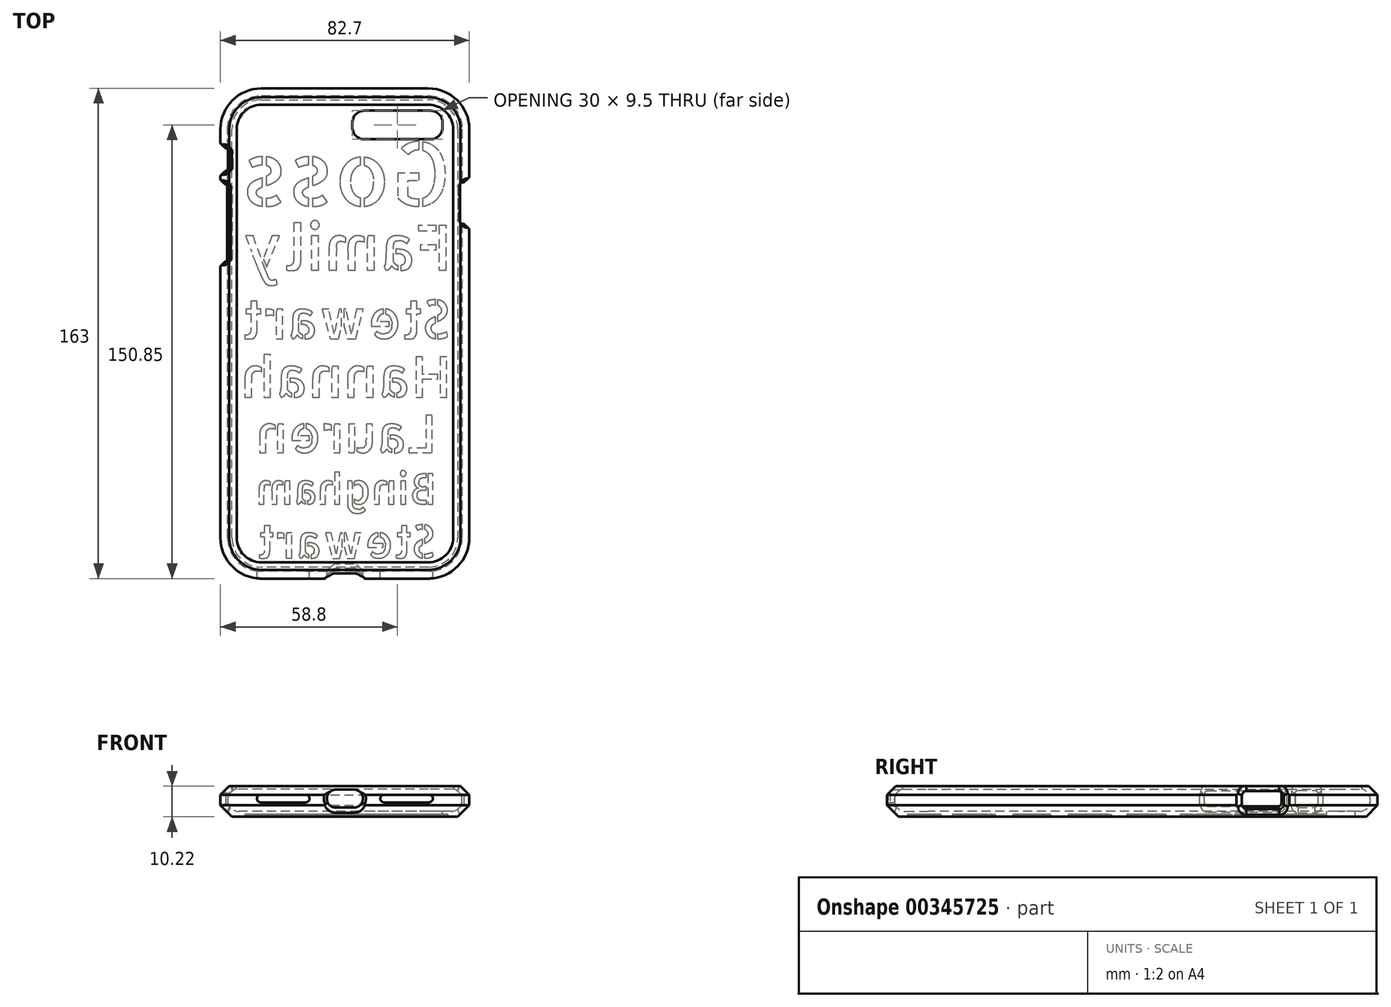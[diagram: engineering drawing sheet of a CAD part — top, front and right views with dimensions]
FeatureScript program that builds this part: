
annotation { "Feature Type Name" : "Feature", "Feature Type Description" : "" }
export const myFeature = defineFeature(function(context is Context, id is Id, definition is map)
    precondition{}
    {
        {
            assignVariable(context, id + "F0", {"name" : "HoleChamferLength", "anyValue" : 1.25});
        }
        {
            assignVariable(context, id + "F1", {"name" : "HoleChamferTopBottom", "anyValue" : 1.75});
        }
        {
            var Q0;
            Q0=qCreatedBy(makeId("Top.planeOp"),FACE);
            var sketch = newSketch(context, id + "F2", { "sketchPlane" : qUnion([Q0])});
            skLineSegment(sketch, "E0.bottom", {"start": v(27.75, 79.1) * mm, "end": v(0, 79.1) * mm});
            skLineSegment(sketch, "E0.top", {"start": v(27.75, -79.1) * mm, "end": v(-27.75, -79.1) * mm});
            skLineSegment(sketch, "E0.left", {"start": v(38.95, 67.9) * mm, "end": v(38.95, -67.9) * mm});
            skLineSegment(sketch, "E0.right", {"start": v(-38.95, 67.9) * mm, "end": v(-38.95, -67.9) * mm});
            skPoint(sketch, "E0.middle", {"position": v(0, 0) * mm});
            skPoint(sketch, "E1.visualSharp", {"position": v(-38.95, 79.1) * mm});
            skArc(sketch, "E1.filletArc", {"start": v(-27.75, 79.1) * mm, "mid": v(-35.67, 75.82) * mm, "end": v(-38.95, 67.9) * mm});
            skPoint(sketch, "E2.visualSharp", {"position": v(38.95, 79.1) * mm});
            skArc(sketch, "E2.filletArc", {"start": v(38.95, 67.9) * mm, "mid": v(35.67, 75.82) * mm, "end": v(27.75, 79.1) * mm});
            skPoint(sketch, "E3.visualSharp", {"position": v(38.95, -79.1) * mm});
            skArc(sketch, "E3.filletArc", {"start": v(27.75, -79.1) * mm, "mid": v(35.67, -75.82) * mm, "end": v(38.95, -67.9) * mm});
            skPoint(sketch, "E4.visualSharp", {"position": v(-38.95, -79.1) * mm});
            skArc(sketch, "E4.filletArc", {"start": v(-38.95, -67.9) * mm, "mid": v(-35.67, -75.82) * mm, "end": v(-27.75, -79.1) * mm});
            skLineSegment(sketch, "E5", {"start": v(0, 79.1) * mm, "end": v(-27.75, 79.1) * mm});
            skSolve(sketch);
        }
        {
            var Q0;
            Q0=qCreatedBy(makeId("Right.planeOp"),FACE);
            var sketch = newSketch(context, id + "F3", { "sketchPlane" : qUnion([Q0])});
            skPoint(sketch, "E6.0", {"position": v(79.1, 0) * mm});
            skArc(sketch, "E7", {"start": v(75.35, -3.75) * mm, "mid": v(79.1, 0) * mm, "end": v(75.35, 3.75) * mm});
            skLineSegment(sketch, "E8", {"start": v(75.35, -3.75) * mm, "end": v(75.35, 3.75) * mm, "construction": true});
            skLineSegment(sketch, "E9", {"start": v(81.5, -1.75) * mm, "end": v(81.5, 1.75) * mm});
            skLineSegment(sketch, "E10", {"start": v(81.5, 1.75) * mm, "end": v(79.75, 3.5) * mm});
            skLineSegment(sketch, "E11.trimOffspring", {"start": v(79.75, -3.5) * mm, "end": v(81.5, -1.75) * mm});
            skLineSegment(sketch, "E12", {"start": v(75.35, -5.55) * mm, "end": v(75.35, -3.75) * mm});
            skLineSegment(sketch, "E13", {"start": v(75.35, -5.55) * mm, "end": v(84.8, -5.55) * mm, "construction": true});
            skPoint(sketch, "E14", {"position": v(81.5, 0) * mm});
            skPoint(sketch, "E15.visualSharp", {"position": v(66.64, 4.7) * mm});
            skArc(sketch, "E15.filletArc", {"start": v(77.32, 4.67) * mm, "mid": v(76.53, 4.4) * mm, "end": v(76.1, 3.67) * mm});
            skLineSegment(sketch, "E16", {"start": v(79.75, -3.5) * mm, "end": v(77.7, -5.55) * mm});
            skLineSegment(sketch, "E17", {"start": v(77.7, -5.55) * mm, "end": v(75.35, -5.55) * mm});
            skLineSegment(sketch, "E18", {"start": v(79.75, 3.5) * mm, "end": v(78.58, 4.67) * mm});
            skLineSegment(sketch, "E19", {"start": v(78.58, 4.67) * mm, "end": v(77.32, 4.67) * mm});
            skLineSegment(sketch, "E20", {"start": v(76.1, 3.67) * mm, "end": v(66.64, 5.6) * mm, "construction": true});
            skSolve(sketch);
        }
        {
            var Q0;
            Q0=sQuery(id+"F2.wireOp",EDGE,"E5");
            var Q1;
            Q1=sQuery(id+"F2.wireOp",VERTEX,"E5.end");
            cPlane(context, id + "F4", {"entities" : qUnion([Q0, Q1]), "cplaneType" : CPlaneType.LINE_POINT, "offset" : 25 * mm, "width" : 150 * mm, "height" : 150 * mm});
        }
        {
            var Q0;
            Q0=sQuery(id+"F2.wireOp",EDGE,"E0.bottom");
            var Q1;
            Q1=sQuery(id+"F2.wireOp",VERTEX,"E2.filletArc.end");
            cPlane(context, id + "F5", {"entities" : qUnion([Q0, Q1]), "cplaneType" : CPlaneType.LINE_POINT, "offset" : 25 * mm, "width" : 150 * mm, "height" : 150 * mm});
        }
        {
            var Q0;
            Q0=sQuery(id+"F2.wireOp",EDGE,"E0.right");
            var Q1;
            Q1=sQuery(id+"F2.wireOp",VERTEX,"E0.right.end");
            cPlane(context, id + "F6", {"entities" : qUnion([Q0, Q1]), "cplaneType" : CPlaneType.LINE_POINT, "offset" : 25 * mm, "width" : 150 * mm, "height" : 150 * mm});
        }
        {
            var Q0;
            Q0=qCreatedBy(id+"F4.planeOp",FACE);
            var sketch = newSketch(context, id + "F7", { "sketchPlane" : qUnion([Q0])});
            skLineSegment(sketch, "E21.bottom", {"start": v(-24.95, -1.88) * mm, "end": v(-48.6, -1.88) * mm});
            skLineSegment(sketch, "E21.top", {"start": v(-24.95, 2.87) * mm, "end": v(-48.6, 2.87) * mm});
            skLineSegment(sketch, "E21.left", {"start": v(-23.95, -0.88) * mm, "end": v(-23.95, 1.87) * mm});
            skLineSegment(sketch, "E21.right", {"start": v(-49.6, -0.88) * mm, "end": v(-49.6, 1.87) * mm});
            skPoint(sketch, "E21.middle", {"position": v(-36.77, 0.5) * mm});
            skPoint(sketch, "E22.visualSharp", {"position": v(-49.6, 2.87) * mm});
            skArc(sketch, "E22.filletArc", {"start": v(-48.6, 2.87) * mm, "mid": v(-49.3, 2.58) * mm, "end": v(-49.6, 1.87) * mm});
            skPoint(sketch, "E23.visualSharp", {"position": v(-49.6, -1.88) * mm});
            skArc(sketch, "E23.filletArc", {"start": v(-49.6, -0.88) * mm, "mid": v(-49.3, -1.58) * mm, "end": v(-48.6, -1.88) * mm});
            skPoint(sketch, "E24.visualSharp", {"position": v(-23.95, 2.87) * mm});
            skArc(sketch, "E24.filletArc", {"start": v(-23.95, 1.87) * mm, "mid": v(-24.24, 2.58) * mm, "end": v(-24.95, 2.87) * mm});
            skPoint(sketch, "E25.visualSharp", {"position": v(-23.95, -1.88) * mm});
            skArc(sketch, "E25.filletArc", {"start": v(-24.95, -1.88) * mm, "mid": v(-24.24, -1.58) * mm, "end": v(-23.95, -0.88) * mm});
            skLineSegment(sketch, "E26.bottom", {"start": v(-60.6, 3.12) * mm, "end": v(-55.1, 3.12) * mm});
            skLineSegment(sketch, "E26.top", {"start": v(-60.6, -2.13) * mm, "end": v(-55.1, -2.13) * mm});
            skLineSegment(sketch, "E26.left", {"start": v(-61.6, 2.12) * mm, "end": v(-61.6, -1.13) * mm});
            skLineSegment(sketch, "E26.right", {"start": v(-54.1, 2.12) * mm, "end": v(-54.1, -1.13) * mm});
            skPoint(sketch, "E26.middle", {"position": v(-57.85, 0.5) * mm});
            skPoint(sketch, "E27.visualSharp", {"position": v(-61.6, 3.12) * mm});
            skArc(sketch, "E27.filletArc", {"start": v(-60.6, 3.13) * mm, "mid": v(-61.3, 2.83) * mm, "end": v(-61.6, 2.12) * mm});
            skPoint(sketch, "E28.visualSharp", {"position": v(-61.6, -2.13) * mm});
            skArc(sketch, "E28.filletArc", {"start": v(-61.6, -1.13) * mm, "mid": v(-61.3, -1.83) * mm, "end": v(-60.6, -2.13) * mm});
            skPoint(sketch, "E29.visualSharp", {"position": v(-54.1, -2.13) * mm});
            skArc(sketch, "E29.filletArc", {"start": v(-55.1, -2.13) * mm, "mid": v(-54.4, -1.83) * mm, "end": v(-54.1, -1.13) * mm});
            skPoint(sketch, "E30.visualSharp", {"position": v(-54.1, 3.12) * mm});
            skArc(sketch, "E30.filletArc", {"start": v(-54.1, 2.12) * mm, "mid": v(-54.4, 2.83) * mm, "end": v(-55.1, 3.13) * mm});
            skSolve(sketch);
        }
        {
            var Q0;
            Q0=qCreatedBy(id+"F5.planeOp",FACE);
            var sketch = newSketch(context, id + "F8", { "sketchPlane" : qUnion([Q0])});
            skLineSegment(sketch, "E31.bottom", {"start": v(-48.85, 2.75) * mm, "end": v(-37.85, 2.75) * mm});
            skLineSegment(sketch, "E31.top", {"start": v(-48.85, -2.75) * mm, "end": v(-37.85, -2.75) * mm});
            skLineSegment(sketch, "E31.left", {"start": v(-50.35, 1.25) * mm, "end": v(-50.35, -1.25) * mm});
            skLineSegment(sketch, "E31.right", {"start": v(-36.35, 1.25) * mm, "end": v(-36.35, -1.25) * mm});
            skPoint(sketch, "E31.middle", {"position": v(-43.35, 0) * mm});
            skPoint(sketch, "E32.visualSharp", {"position": v(-50.35, 2.75) * mm});
            skArc(sketch, "E32.filletArc", {"start": v(-48.85, 2.75) * mm, "mid": v(-49.91, 2.31) * mm, "end": v(-50.35, 1.25) * mm});
            skPoint(sketch, "E33.visualSharp", {"position": v(-50.35, -2.75) * mm});
            skArc(sketch, "E33.filletArc", {"start": v(-50.35, -1.25) * mm, "mid": v(-49.91, -2.31) * mm, "end": v(-48.85, -2.75) * mm});
            skPoint(sketch, "E34.visualSharp", {"position": v(-36.35, -2.75) * mm});
            skArc(sketch, "E34.filletArc", {"start": v(-37.85, -2.75) * mm, "mid": v(-36.79, -2.31) * mm, "end": v(-36.35, -1.25) * mm});
            skPoint(sketch, "E35.visualSharp", {"position": v(-36.35, 2.75) * mm});
            skArc(sketch, "E35.filletArc", {"start": v(-36.35, 1.25) * mm, "mid": v(-36.79, 2.31) * mm, "end": v(-37.85, 2.75) * mm});
            skSolve(sketch);
        }
        {
            var Q0;
            Q0=qCreatedBy(id+"F6.planeOp",FACE);
            var sketch = newSketch(context, id + "F9", { "sketchPlane" : qUnion([Q0])});
            skLineSegment(sketch, "E36.bottom", {"start": v(3, 3.5) * mm, "end": v(-3, 3.5) * mm});
            skLineSegment(sketch, "E36.top", {"start": v(3, -2.5) * mm, "end": v(-3, -2.5) * mm});
            skLineSegment(sketch, "E36.left", {"start": v(6, 0.5) * mm, "end": v(6, 0.5) * mm});
            skLineSegment(sketch, "E36.right", {"start": v(-6, 0.5) * mm, "end": v(-6, 0.5) * mm});
            skPoint(sketch, "E36.middle", {"position": v(0, 0.5) * mm});
            skPoint(sketch, "E37.visualSharp", {"position": v(-6, 3.5) * mm});
            skArc(sketch, "E37.filletArc", {"start": v(-3, 3.5) * mm, "mid": v(-5.12, 2.62) * mm, "end": v(-6, 0.5) * mm});
            skPoint(sketch, "E38.visualSharp", {"position": v(-6, -2.5) * mm});
            skArc(sketch, "E38.filletArc", {"start": v(-6, 0.5) * mm, "mid": v(-5.12, -1.62) * mm, "end": v(-3, -2.5) * mm});
            skPoint(sketch, "E39.visualSharp", {"position": v(6, -2.5) * mm});
            skArc(sketch, "E39.filletArc", {"start": v(3, -2.5) * mm, "mid": v(5.12, -1.62) * mm, "end": v(6, 0.5) * mm});
            skPoint(sketch, "E40.visualSharp", {"position": v(6, 3.5) * mm});
            skArc(sketch, "E40.filletArc", {"start": v(6, 0.5) * mm, "mid": v(5.12, 2.62) * mm, "end": v(3, 3.5) * mm});
            skLineSegment(sketch, "E41", {"start": v(13, 0.5) * mm, "end": v(28, 0.5) * mm, "construction": true});
            skArc(sketch, "E42.0.startCap", {"start": v(13, -0.75) * mm, "mid": v(11.75, 0.5) * mm, "end": v(13, 1.75) * mm});
            skArc(sketch, "E42.0.endCap", {"start": v(28, 1.75) * mm, "mid": v(29.25, 0.5) * mm, "end": v(28, -0.75) * mm});
            skLineSegment(sketch, "E42.0.left", {"start": v(13, 1.75) * mm, "end": v(28, 1.75) * mm});
            skLineSegment(sketch, "E42.0.right", {"start": v(13, -0.75) * mm, "end": v(28, -0.75) * mm});
            skLineSegment(sketch, "E43", {"start": v(0, 0.5) * mm, "end": v(0, -2.5) * mm, "construction": true});
            skArc(sketch, "E44.MirrorCS", {"start": v(13, 1.75) * mm, "mid": v(11.75, 0.5) * mm, "end": v(13, -0.75) * mm});
            skArc(sketch, "E45.MirrorCS", {"start": v(28, -0.75) * mm, "mid": v(29.25, 0.5) * mm, "end": v(28, 1.75) * mm});
            skLineSegment(sketch, "E46.MirrorCS", {"start": v(0, 0.5) * mm, "end": v(0, 3.5) * mm, "construction": true});
            skArc(sketch, "E47.MirrorCS", {"start": v(-28, -0.75) * mm, "mid": v(-29.25, 0.5) * mm, "end": v(-28, 1.75) * mm});
            skLineSegment(sketch, "E48.MirrorCS", {"start": v(-13, 1.75) * mm, "end": v(-28, 1.75) * mm});
            skLineSegment(sketch, "E49.MirrorCS", {"start": v(-13, -0.75) * mm, "end": v(-28, -0.75) * mm});
            skArc(sketch, "E50.MirrorCS", {"start": v(-13, 1.75) * mm, "mid": v(-11.75, 0.5) * mm, "end": v(-13, -0.75) * mm});
            skArc(sketch, "E51.MirrorCS", {"start": v(-13, -0.75) * mm, "mid": v(-11.75, 0.5) * mm, "end": v(-13, 1.75) * mm});
            skArc(sketch, "E52.MirrorCS", {"start": v(-28, 1.75) * mm, "mid": v(-29.25, 0.5) * mm, "end": v(-28, -0.75) * mm});
            skLineSegment(sketch, "E53.MirrorCS", {"start": v(-13, 0.5) * mm, "end": v(-28, 0.5) * mm, "construction": true});
            skSolve(sketch);
        }
        {
            var Q0;
            Q0=qCreatedBy(makeId("Top.planeOp"),FACE);
            var sketch = newSketch(context, id + "F10", { "sketchPlane" : qUnion([Q0])});
            skLineSegment(sketch, "E54.bottom", {"start": v(28.45, 64.6) * mm, "end": v(6.45, 64.6) * mm});
            skLineSegment(sketch, "E54.top", {"start": v(28.45, 74.1) * mm, "end": v(6.45, 74.1) * mm});
            skLineSegment(sketch, "E54.left", {"start": v(32.45, 68.6) * mm, "end": v(32.45, 70.1) * mm});
            skLineSegment(sketch, "E54.right", {"start": v(2.45, 68.6) * mm, "end": v(2.45, 70.1) * mm});
            skPoint(sketch, "E54.middle", {"position": v(17.45, 69.35) * mm});
            skPoint(sketch, "E55.visualSharp", {"position": v(2.45, 74.1) * mm});
            skArc(sketch, "E55.filletArc", {"start": v(6.45, 74.1) * mm, "mid": v(3.62, 72.93) * mm, "end": v(2.45, 70.1) * mm});
            skPoint(sketch, "E56.visualSharp", {"position": v(2.45, 64.6) * mm});
            skArc(sketch, "E56.filletArc", {"start": v(2.45, 68.6) * mm, "mid": v(3.62, 65.77) * mm, "end": v(6.45, 64.6) * mm});
            skPoint(sketch, "E57.visualSharp", {"position": v(32.45, 64.6) * mm});
            skArc(sketch, "E57.filletArc", {"start": v(28.45, 64.6) * mm, "mid": v(31.28, 65.77) * mm, "end": v(32.45, 68.6) * mm});
            skPoint(sketch, "E58.visualSharp", {"position": v(32.45, 74.1) * mm});
            skArc(sketch, "E58.filletArc", {"start": v(32.45, 70.1) * mm, "mid": v(31.28, 72.93) * mm, "end": v(28.45, 74.1) * mm});
            skSolve(sketch);
        }
        {
            var Q0;
            Q0=qSketchRegion(id+"F3",true);
            var Q1;
            Q1=sQuery(id+"F2.wireOp",EDGE,"E5");
            var Q2;
            Q2=sQuery(id+"F2.wireOp",EDGE,"E1.filletArc");
            var Q3;
            Q3=sQuery(id+"F2.wireOp",EDGE,"E0.right");
            var Q4;
            Q4=sQuery(id+"F2.wireOp",EDGE,"E4.filletArc");
            var Q5;
            Q5=sQuery(id+"F2.wireOp",EDGE,"E0.top");
            var Q6;
            Q6=sQuery(id+"F2.wireOp",EDGE,"E3.filletArc");
            var Q7;
            Q7=sQuery(id+"F2.wireOp",EDGE,"E0.left");
            var Q8;
            Q8=sQuery(id+"F2.wireOp",EDGE,"E2.filletArc");
            var Q9;
            Q9=sQuery(id+"F2.wireOp",EDGE,"E0.bottom");
            sweep(context, id + "F11", {"profiles" : qUnion([Q0]), "path" : qUnion([Q1, Q2, Q3, Q4, Q5, Q6, Q7, Q8, Q9])});
        }
        {
            var Q0;
            Q0=qCreatedBy(makeId("Front.planeOp"),FACE);
            var sketch = newSketch(context, id + "F12", { "sketchPlane" : qUnion([Q0])});
            skLineSegment(sketch, "E59.0.0", {"start": v(35.2, -5.55) * mm, "end": v(27.75, -5.55) * mm});
            skLineSegment(sketch, "E59.0.1", {"start": v(27.75, -3.75) * mm, "end": v(27.75, -5.55) * mm});
            skLineSegment(sketch, "E59.0.2", {"start": v(27.75, -3.75) * mm, "end": v(35.2, -3.75) * mm});
            skLineSegment(sketch, "E59.0.3", {"start": v(35.2, -3.75) * mm, "end": v(35.2, -5.55) * mm});
            skLineSegment(sketch, "E59.1.0", {"start": v(27.75, -5.55) * mm, "end": v(-27.75, -5.55) * mm});
            skLineSegment(sketch, "E59.1.1", {"start": v(-27.75, -3.75) * mm, "end": v(-27.75, -5.55) * mm});
            skLineSegment(sketch, "E59.1.2", {"start": v(-27.75, -3.75) * mm, "end": v(27.75, -3.75) * mm});
            skLineSegment(sketch, "E59.1.3", {"start": v(27.75, -3.75) * mm, "end": v(27.75, -5.55) * mm});
            skLineSegment(sketch, "E59.2.0", {"start": v(-27.75, -5.55) * mm, "end": v(-35.2, -5.55) * mm});
            skLineSegment(sketch, "E59.2.1", {"start": v(-35.2, -3.75) * mm, "end": v(-35.2, -5.55) * mm});
            skLineSegment(sketch, "E59.2.2", {"start": v(-35.2, -3.75) * mm, "end": v(-27.75, -3.75) * mm});
            skLineSegment(sketch, "E59.2.3", {"start": v(-27.75, -3.75) * mm, "end": v(-27.75, -5.55) * mm});
            skSolve(sketch);
        }
        {
            var Q0;
            Q0=qSketchRegion(id+"F12",true);
            extrude(context, id + "F13", {"entities" : qUnion([Q0]), "operationType" : NewBodyOperationType.ADD, "endBound" : BoundingType.UP_TO_NEXT, "depth" : 25 * mm, "hasSecondDirection" : true, "secondDirectionBound" : SecondDirectionBoundingType.UP_TO_NEXT, "secondDirectionOppositeDirection" : true, "secondDirectionDepth" : 25 * mm});
        }
        {
            var Q0;
            Q0=qSketchRegion(id+"F7",true);
            extrude(context, id + "F14", {"entities" : qUnion([Q0]), "operationType" : NewBodyOperationType.REMOVE, "endBound" : BoundingType.THROUGH_ALL, "depth" : 25 * mm});
        }
        {
            var Q0;
            Q0=qSketchRegion(id+"F8",true);
            extrude(context, id + "F15", {"entities" : qUnion([Q0]), "operationType" : NewBodyOperationType.REMOVE, "endBound" : BoundingType.THROUGH_ALL, "oppositeDirection" : true, "depth" : 25 * mm});
        }
        {
            var Q0;
            Q0=makeQuery(id+"F10.imprint","IMPRINT",FACE,{"disambiguationData":[TD([[makeQuery(id+"F10.imprint","IMPRINT",EDGE,{"derivedFrom":sQuery(id+"F10.wireOp",EDGE,"E54.bottom")}),-1.0]])]});
            extrude(context, id + "F16", {"entities" : qUnion([Q0]), "operationType" : NewBodyOperationType.REMOVE, "endBound" : BoundingType.THROUGH_ALL, "oppositeDirection" : true, "depth" : 25 * mm});
        }
        {
            var Q0;
            Q0=qSketchRegion(id+"F9",true);
            extrude(context, id + "F17", {"entities" : qUnion([Q0]), "operationType" : NewBodyOperationType.REMOVE, "endBound" : BoundingType.THROUGH_ALL, "depth" : 25 * mm});
        }
        {
            var Q0;
            Q0=makeQuery(id+"F14.boolean.opBoolean","INTERSECT",EDGE,{"derivedFrom":[makeQuery(id+"F11.opSweep","SWEPT_FACE",FACE,{"disambiguationData":[OSD([sQuery(id+"F2.wireOp",EDGE,"E0.right"),sQuery(id+"F3.wireOp",EDGE,"E11.trimOffspring"),sQuery(id+"F3.wireOp",EDGE,"E16")])]}),makeQuery(id+"F14.opExtrude","SWEPT_FACE",FACE,{"disambiguationData":[OSD([sQuery(id+"F7.wireOp",EDGE,"E21.bottom")])]})]});
            var Q1;
            Q1=makeQuery(id+"F14.boolean.opBoolean","INTERSECT",EDGE,{"derivedFrom":[makeQuery(id+"F11.opSweep","SWEPT_FACE",FACE,{"disambiguationData":[OSD([sQuery(id+"F2.wireOp",EDGE,"E0.right"),sQuery(id+"F3.wireOp",EDGE,"E10")])]}),makeQuery(id+"F14.opExtrude","SWEPT_FACE",FACE,{"disambiguationData":[OSD([sQuery(id+"F7.wireOp",EDGE,"E21.top")])]})]});
            chamfer(context, id + "F18", {"entities" : qUnion([Q0, Q1]), "width" : (getVariable(context, 'HoleChamferLength')) * mm, "tangentPropagation" : true});
        }
        {
            var Q0;
            Q0=makeQuery(id+"F14.boolean.opBoolean","INTERSECT",EDGE,{"derivedFrom":[makeQuery(id+"F11.opSweep","SWEPT_FACE",FACE,{"disambiguationData":[OSD([sQuery(id+"F2.wireOp",EDGE,"E0.right"),sQuery(id+"F3.wireOp",EDGE,"E11.trimOffspring"),sQuery(id+"F3.wireOp",EDGE,"E16")])]}),makeQuery(id+"F14.opExtrude","SWEPT_FACE",FACE,{"disambiguationData":[OSD([sQuery(id+"F7.wireOp",EDGE,"E26.top")])]})]});
            var Q1;
            Q1=makeQuery(id+"F14.boolean.opBoolean","INTERSECT",EDGE,{"derivedFrom":[makeQuery(id+"F11.opSweep","SWEPT_FACE",FACE,{"disambiguationData":[OSD([sQuery(id+"F2.wireOp",EDGE,"E0.right"),sQuery(id+"F3.wireOp",EDGE,"E10")])]}),makeQuery(id+"F14.opExtrude","SWEPT_FACE",FACE,{"disambiguationData":[OSD([sQuery(id+"F7.wireOp",EDGE,"E26.bottom")])]})]});
            chamfer(context, id + "F19", {"entities" : qUnion([Q0, Q1]), "width" : (getVariable(context, 'HoleChamferLength')) * mm, "tangentPropagation" : true});
        }
        {
            var Q0;
            Q0=makeQuery(id+"F15.boolean.opBoolean","INTERSECT",EDGE,{"derivedFrom":[makeQuery(id+"F11.opSweep","SWEPT_FACE",FACE,{"disambiguationData":[OSD([sQuery(id+"F2.wireOp",EDGE,"E0.left"),sQuery(id+"F3.wireOp",EDGE,"E11.trimOffspring"),sQuery(id+"F3.wireOp",EDGE,"E16")])]}),makeQuery(id+"F15.opExtrude","SWEPT_FACE",FACE,{"disambiguationData":[OSD([sQuery(id+"F8.wireOp",EDGE,"E31.top")])]})]});
            var Q1;
            Q1=makeQuery(id+"F15.boolean.opBoolean","INTERSECT",EDGE,{"derivedFrom":[makeQuery(id+"F11.opSweep","SWEPT_FACE",FACE,{"disambiguationData":[OSD([sQuery(id+"F2.wireOp",EDGE,"E0.left"),sQuery(id+"F3.wireOp",EDGE,"E10")])]}),makeQuery(id+"F15.opExtrude","SWEPT_FACE",FACE,{"disambiguationData":[OSD([sQuery(id+"F8.wireOp",EDGE,"E31.bottom")])]})]});
            chamfer(context, id + "F20", {"entities" : qUnion([Q0, Q1]), "width" : (getVariable(context, 'HoleChamferLength')) * mm, "tangentPropagation" : true});
        }
        {
            var Q0;
            Q0=makeQuery(id+"F15.boolean.opBoolean","INTERSECT",EDGE,{"derivedFrom":[makeQuery(id+"F11.opSweep","SWEPT_FACE",FACE,{"disambiguationData":[OSD([sQuery(id+"F2.wireOp",EDGE,"E0.left"),sQuery(id+"F3.wireOp",EDGE,"E9")])]}),makeQuery(id+"F15.opExtrude","SWEPT_FACE",FACE,{"disambiguationData":[OSD([sQuery(id+"F8.wireOp",EDGE,"E31.left")])]})]});
            var Q1;
            Q1=makeQuery(id+"F15.boolean.opBoolean","INTERSECT",EDGE,{"derivedFrom":[makeQuery(id+"F11.opSweep","SWEPT_FACE",FACE,{"disambiguationData":[OSD([sQuery(id+"F2.wireOp",EDGE,"E0.left"),sQuery(id+"F3.wireOp",EDGE,"E9")])]}),makeQuery(id+"F15.opExtrude","SWEPT_FACE",FACE,{"disambiguationData":[OSD([sQuery(id+"F8.wireOp",EDGE,"E31.right")])]})]});
            var Q2;
            Q2=makeQuery(id+"F14.boolean.opBoolean","INTERSECT",EDGE,{"derivedFrom":[makeQuery(id+"F11.opSweep","SWEPT_FACE",FACE,{"disambiguationData":[OSD([sQuery(id+"F2.wireOp",EDGE,"E0.right"),sQuery(id+"F3.wireOp",EDGE,"E9")])]}),makeQuery(id+"F14.opExtrude","SWEPT_FACE",FACE,{"disambiguationData":[OSD([sQuery(id+"F7.wireOp",EDGE,"E21.left")])]})]});
            var Q3;
            Q3=makeQuery(id+"F14.boolean.opBoolean","INTERSECT",EDGE,{"derivedFrom":[makeQuery(id+"F11.opSweep","SWEPT_FACE",FACE,{"disambiguationData":[OSD([sQuery(id+"F2.wireOp",EDGE,"E0.right"),sQuery(id+"F3.wireOp",EDGE,"E9")])]}),makeQuery(id+"F14.opExtrude","SWEPT_FACE",FACE,{"disambiguationData":[OSD([sQuery(id+"F7.wireOp",EDGE,"E21.right")])]})]});
            var Q4;
            Q4=makeQuery(id+"F14.boolean.opBoolean","INTERSECT",EDGE,{"derivedFrom":[makeQuery(id+"F11.opSweep","SWEPT_FACE",FACE,{"disambiguationData":[OSD([sQuery(id+"F2.wireOp",EDGE,"E0.right"),sQuery(id+"F3.wireOp",EDGE,"E9")])]}),makeQuery(id+"F14.opExtrude","SWEPT_FACE",FACE,{"disambiguationData":[OSD([sQuery(id+"F7.wireOp",EDGE,"E26.left")])]})]});
            var Q5;
            Q5=makeQuery(id+"F14.boolean.opBoolean","INTERSECT",EDGE,{"derivedFrom":[makeQuery(id+"F11.opSweep","SWEPT_FACE",FACE,{"disambiguationData":[OSD([sQuery(id+"F2.wireOp",EDGE,"E0.right"),sQuery(id+"F3.wireOp",EDGE,"E9")])]}),makeQuery(id+"F14.opExtrude","SWEPT_FACE",FACE,{"disambiguationData":[OSD([sQuery(id+"F7.wireOp",EDGE,"E26.right")])]})]});
            chamfer(context, id + "F21", {"entities" : qUnion([Q0, Q1, Q2, Q3, Q4, Q5]), "width" : (getVariable(context, 'HoleChamferTopBottom')) * mm, "tangentPropagation" : true});
        }
        {
            var Q0;
            Q0=makeQuery(id+"F17.boolean.opBoolean","INTERSECT",EDGE,{"derivedFrom":[makeQuery(id+"F11.opSweep","SWEPT_FACE",FACE,{"disambiguationData":[OSD([sQuery(id+"F2.wireOp",EDGE,"E0.top"),sQuery(id+"F3.wireOp",EDGE,"E11.trimOffspring"),sQuery(id+"F3.wireOp",EDGE,"E16")])]}),makeQuery(id+"F17.opExtrude","SWEPT_FACE",FACE,{"disambiguationData":[OSD([sQuery(id+"F9.wireOp",EDGE,"E36.top")])]})]});
            var Q1;
            Q1=makeQuery(id+"F17.boolean.opBoolean","INTERSECT",EDGE,{"derivedFrom":[makeQuery(id+"F11.opSweep","SWEPT_FACE",FACE,{"disambiguationData":[OSD([sQuery(id+"F2.wireOp",EDGE,"E0.top"),sQuery(id+"F3.wireOp",EDGE,"E9")])]}),makeQuery(id+"F17.opExtrude","SWEPT_FACE",FACE,{"disambiguationData":[OSD([sQuery(id+"F9.wireOp",EDGE,"E37.filletArc"),sQuery(id+"F9.wireOp",EDGE,"E38.filletArc")])]})]});
            var Q2;
            Q2=makeQuery(id+"F17.boolean.opBoolean","INTERSECT",EDGE,{"derivedFrom":[makeQuery(id+"F11.opSweep","SWEPT_FACE",FACE,{"disambiguationData":[OSD([sQuery(id+"F2.wireOp",EDGE,"E0.top"),sQuery(id+"F3.wireOp",EDGE,"E9")])]}),makeQuery(id+"F17.opExtrude","SWEPT_FACE",FACE,{"disambiguationData":[OSD([sQuery(id+"F9.wireOp",EDGE,"E39.filletArc"),sQuery(id+"F9.wireOp",EDGE,"E40.filletArc")])]})]});
            chamfer(context, id + "F22", {"entities" : qUnion([Q0, Q1, Q2]), "width" : 1 * mm, "tangentPropagation" : true});
        }
        {
            var Q0;
            Q0=qCreatedBy(makeId("Right.planeOp"),FACE);
            var sketch = newSketch(context, id + "F23", { "sketchPlane" : qUnion([Q0])});
            skLineSegment(sketch, "E60", {"start": v(73.83, -4.65) * mm, "end": v(73.23, -4.65) * mm});
            skLineSegment(sketch, "E61", {"start": v(72.71, -5.55) * mm, "end": v(74.35, -5.55) * mm});
            skLineSegment(sketch, "E62", {"start": v(74.35, -5.55) * mm, "end": v(73.83, -4.65) * mm});
            skLineSegment(sketch, "E63", {"start": v(73.23, -4.65) * mm, "end": v(72.71, -5.55) * mm});
            skSolve(sketch);
        }
        {
            var Q0;
            Q0=makeQuery(id+"F13.boolean.opBoolean","MERGE",FACE,{"derivedFrom":[makeQuery(id+"F11.opSweep","SWEPT_FACE",FACE,{"disambiguationData":[OSD([sQuery(id+"F2.wireOp",EDGE,"E0.bottom"),sQuery(id+"F3.wireOp",EDGE,"E17")])]}),makeQuery(id+"F13.opExtrude","SWEPT_FACE",FACE,{"disambiguationData":[OSD([sQuery(id+"F12.wireOp",EDGE,"E59.0.0"),sQuery(id+"F12.wireOp",EDGE,"E59.1.0"),sQuery(id+"F12.wireOp",EDGE,"E59.2.0")])]})]});
            cPlane(context, id + "F24", {"entities" : qUnion([Q0]), "cplaneType" : CPlaneType.OFFSET, "offset" : 1.4 * mm, "oppositeDirection" : true, "width" : 150 * mm, "height" : 150 * mm});
        }
        {
            var Q0;
            Q0=makeQuery(id+"F13.boolean.opBoolean","MERGE",FACE,{"derivedFrom":[makeQuery(id+"F11.opSweep","SWEPT_FACE",FACE,{"disambiguationData":[OSD([sQuery(id+"F2.wireOp",EDGE,"E0.bottom"),sQuery(id+"F3.wireOp",EDGE,"E17")])]}),makeQuery(id+"F13.opExtrude","SWEPT_FACE",FACE,{"disambiguationData":[OSD([sQuery(id+"F12.wireOp",EDGE,"E59.0.0"),sQuery(id+"F12.wireOp",EDGE,"E59.1.0"),sQuery(id+"F12.wireOp",EDGE,"E59.2.0")])]})]});
            var sketch = newSketch(context, id + "F25", { "sketchPlane" : qUnion([Q0])});
            skText(sketch, "E64", { "text": "Goss", "fontName": "AllertaStencil-Regular.ttf"});
            skLineSegment(sketch, "E65", {"start": v(32.5, -8.36) * mm, "end": v(-36.29, -8.36) * mm, "construction": true});
            skText(sketch, "E66", { "text": "Family", "fontName": "AllertaStencil-Regular.ttf"});
            const initialGuessF25  = {"E64": [0.03564, -0.04239, -1, 0, 0.02114], "E66": [0.03564, -0.02105, -1, 0, 0.01491]};
            skSetInitialGuess(sketch, initialGuessF25);
            skSolve(sketch);
        }
        {
            var Q0;
            Q0 = qSketchRegion(id + "F25", true);
            extrude(context, id + "F26", {"entities" : qUnion([Q0]), "operationType" : NewBodyOperationType.REMOVE, "oppositeDirection" : true, "depth" : 0.75 * mm});
        }
        {
            var Q0;
            Q0=makeQuery(id+"F13.boolean.opBoolean","MERGE",FACE,{"derivedFrom":[makeQuery(id+"F11.opSweep","SWEPT_FACE",FACE,{"disambiguationData":[OSD([sQuery(id+"F2.wireOp",EDGE,"E0.bottom"),sQuery(id+"F3.wireOp",EDGE,"E17")])]}),makeQuery(id+"F13.opExtrude","SWEPT_FACE",FACE,{"disambiguationData":[OSD([sQuery(id+"F12.wireOp",EDGE,"E59.0.0"),sQuery(id+"F12.wireOp",EDGE,"E59.1.0"),sQuery(id+"F12.wireOp",EDGE,"E59.2.0")])]})]});
            var sketch = newSketch(context, id + "F27", { "sketchPlane" : qUnion([Q0])});
            skLineSegment(sketch, "E67", {"start": v(34.34, -0.67) * mm, "end": v(32.85, 0) * mm});
            skLineSegment(sketch, "E68", {"start": v(32.85, 0) * mm, "end": v(27.19, -12.6) * mm});
            skLineSegment(sketch, "E69", {"start": v(27.19, -12.6) * mm, "end": v(28.68, -13.27) * mm});
            skLineSegment(sketch, "E70", {"start": v(28.68, -13.27) * mm, "end": v(34.34, -0.67) * mm});
            skLineSegment(sketch, "E71", {"start": v(34.34, -6.97) * mm, "end": v(-31.37, -6.97) * mm, "construction": true});
            skPoint(sketch, "E71.startSnap0", {"position": v(31.5, -6.97) * mm});
            skLineSegment(sketch, "E72.1.0.0", {"start": v(21.78, -13.27) * mm, "end": v(27.44, -0.67) * mm});
            skLineSegment(sketch, "E72.1.0.1", {"start": v(25.95, 0) * mm, "end": v(20.29, -12.6) * mm});
            skLineSegment(sketch, "E72.1.0.2", {"start": v(27.44, -0.67) * mm, "end": v(25.95, 0) * mm});
            skLineSegment(sketch, "E72.1.0.3", {"start": v(20.29, -12.6) * mm, "end": v(21.78, -13.27) * mm});
            skLineSegment(sketch, "E72.2.0.0", {"start": v(14.88, -13.27) * mm, "end": v(20.54, -0.67) * mm});
            skLineSegment(sketch, "E72.2.0.1", {"start": v(19.05, 0) * mm, "end": v(13.39, -12.6) * mm});
            skLineSegment(sketch, "E72.2.0.2", {"start": v(20.54, -0.67) * mm, "end": v(19.05, 0) * mm});
            skLineSegment(sketch, "E72.2.0.3", {"start": v(13.39, -12.6) * mm, "end": v(14.88, -13.27) * mm});
            skLineSegment(sketch, "E72.3.0.0", {"start": v(7.98, -13.27) * mm, "end": v(13.64, -0.67) * mm});
            skLineSegment(sketch, "E72.3.0.1", {"start": v(12.15, 0) * mm, "end": v(6.49, -12.6) * mm});
            skLineSegment(sketch, "E72.3.0.2", {"start": v(13.64, -0.67) * mm, "end": v(12.15, 0) * mm});
            skLineSegment(sketch, "E72.3.0.3", {"start": v(6.49, -12.6) * mm, "end": v(7.98, -13.27) * mm});
            skLineSegment(sketch, "E72.4.0.0", {"start": v(1.08, -13.27) * mm, "end": v(6.74, -0.67) * mm});
            skLineSegment(sketch, "E72.4.0.1", {"start": v(5.25, 0) * mm, "end": v(-0.41, -12.6) * mm});
            skLineSegment(sketch, "E72.4.0.2", {"start": v(6.74, -0.67) * mm, "end": v(5.25, 0) * mm});
            skLineSegment(sketch, "E72.4.0.3", {"start": v(-0.41, -12.6) * mm, "end": v(1.08, -13.27) * mm});
            skLineSegment(sketch, "E72.5.0.0", {"start": v(-5.82, -13.27) * mm, "end": v(-0.16, -0.67) * mm});
            skLineSegment(sketch, "E72.5.0.1", {"start": v(-1.65, 0) * mm, "end": v(-7.31, -12.6) * mm});
            skLineSegment(sketch, "E72.5.0.2", {"start": v(-0.16, -0.67) * mm, "end": v(-1.65, 0) * mm});
            skLineSegment(sketch, "E72.5.0.3", {"start": v(-7.31, -12.6) * mm, "end": v(-5.82, -13.27) * mm});
            skLineSegment(sketch, "E72.6.0.0", {"start": v(-12.72, -13.27) * mm, "end": v(-7.06, -0.67) * mm});
            skLineSegment(sketch, "E72.6.0.1", {"start": v(-8.55, 0) * mm, "end": v(-14.21, -12.6) * mm});
            skLineSegment(sketch, "E72.6.0.2", {"start": v(-7.06, -0.67) * mm, "end": v(-8.55, 0) * mm});
            skLineSegment(sketch, "E72.6.0.3", {"start": v(-14.21, -12.6) * mm, "end": v(-12.72, -13.27) * mm});
            skLineSegment(sketch, "E72.7.0.0", {"start": v(-19.62, -13.27) * mm, "end": v(-13.96, -0.67) * mm});
            skLineSegment(sketch, "E72.7.0.1", {"start": v(-15.45, 0) * mm, "end": v(-21.11, -12.6) * mm});
            skLineSegment(sketch, "E72.7.0.2", {"start": v(-13.96, -0.67) * mm, "end": v(-15.45, 0) * mm});
            skLineSegment(sketch, "E72.7.0.3", {"start": v(-21.11, -12.6) * mm, "end": v(-19.62, -13.27) * mm});
            skLineSegment(sketch, "E72.8.0.0", {"start": v(-26.52, -13.27) * mm, "end": v(-20.86, -0.67) * mm});
            skLineSegment(sketch, "E72.8.0.1", {"start": v(-22.35, 0) * mm, "end": v(-28.01, -12.6) * mm});
            skLineSegment(sketch, "E72.8.0.2", {"start": v(-20.86, -0.67) * mm, "end": v(-22.35, 0) * mm});
            skLineSegment(sketch, "E72.8.0.3", {"start": v(-28.01, -12.6) * mm, "end": v(-26.52, -13.27) * mm});
            skLineSegment(sketch, "E72.9.0.0", {"start": v(-33.42, -13.27) * mm, "end": v(-27.76, -0.67) * mm});
            skLineSegment(sketch, "E72.9.0.1", {"start": v(-29.25, 0) * mm, "end": v(-34.91, -12.6) * mm});
            skLineSegment(sketch, "E72.9.0.2", {"start": v(-27.76, -0.67) * mm, "end": v(-29.25, 0) * mm});
            skLineSegment(sketch, "E72.9.0.3", {"start": v(-34.91, -12.6) * mm, "end": v(-33.42, -13.27) * mm});
            skLineSegment(sketch, "E72.direction1", {"start": v(28.68, -13.27) * mm, "end": v(21.78, -13.27) * mm, "construction": true});
            skSolve(sketch);
        }
        {
            var Q0;
            Q0=makeQuery(id+"F13.boolean.opBoolean","MERGE",FACE,{"derivedFrom":[makeQuery(id+"F11.opSweep","SWEPT_FACE",FACE,{"disambiguationData":[OSD([sQuery(id+"F2.wireOp",EDGE,"E0.bottom"),sQuery(id+"F3.wireOp",EDGE,"E17")])]}),makeQuery(id+"F13.opExtrude","SWEPT_FACE",FACE,{"disambiguationData":[OSD([sQuery(id+"F12.wireOp",EDGE,"E59.0.0"),sQuery(id+"F12.wireOp",EDGE,"E59.1.0"),sQuery(id+"F12.wireOp",EDGE,"E59.2.0")])]})]});
            var sketch = newSketch(context, id + "F28", { "sketchPlane" : qUnion([Q0])});
            skText(sketch, "E73", { "text": "Stewart", "fontName": "AllertaStencil-Regular.ttf"});
            skText(sketch, "E74", { "text": "Hannah", "fontName": "AllertaStencil-Regular.ttf"});
            skText(sketch, "E75", { "text": "Lauren", "fontName": "AllertaStencil-Regular.ttf"});
            skText(sketch, "E76", { "text": "Bingham", "fontName": "AllertaStencil-Regular.ttf"});
            skText(sketch, "E77", { "text": "Stewart", "fontName": "AllertaStencil-Regular.ttf"});
            const initialGuessF28  = {"E73": [0.03555, 0.00174, -1, 0, 0.0128], "E74": [0.03555, 0.02118, -1, 0, 0.01345], "E75": [0.03055, 0.03965, -1, 0, 0.01247], "E76": [0.03055, 0.05673, -1, 0, 0.01008], "E77": [0.03055, 0.0747, -1, 0, 0.01097]};
            skSetInitialGuess(sketch, initialGuessF28);
            skSolve(sketch);
        }
        {
            var Q0;
            Q0 = qSketchRegion(id + "F28", true);
            extrude(context, id + "F29", {"entities" : qUnion([Q0]), "operationType" : NewBodyOperationType.REMOVE, "flatOperationType" : FlatOperationType.REMOVE, "oppositeDirection" : true, "offsetDistance" : 25 * mm, "depth" : 0.75 * mm, "domain" : OperationDomain.MODEL});
        }
    });
